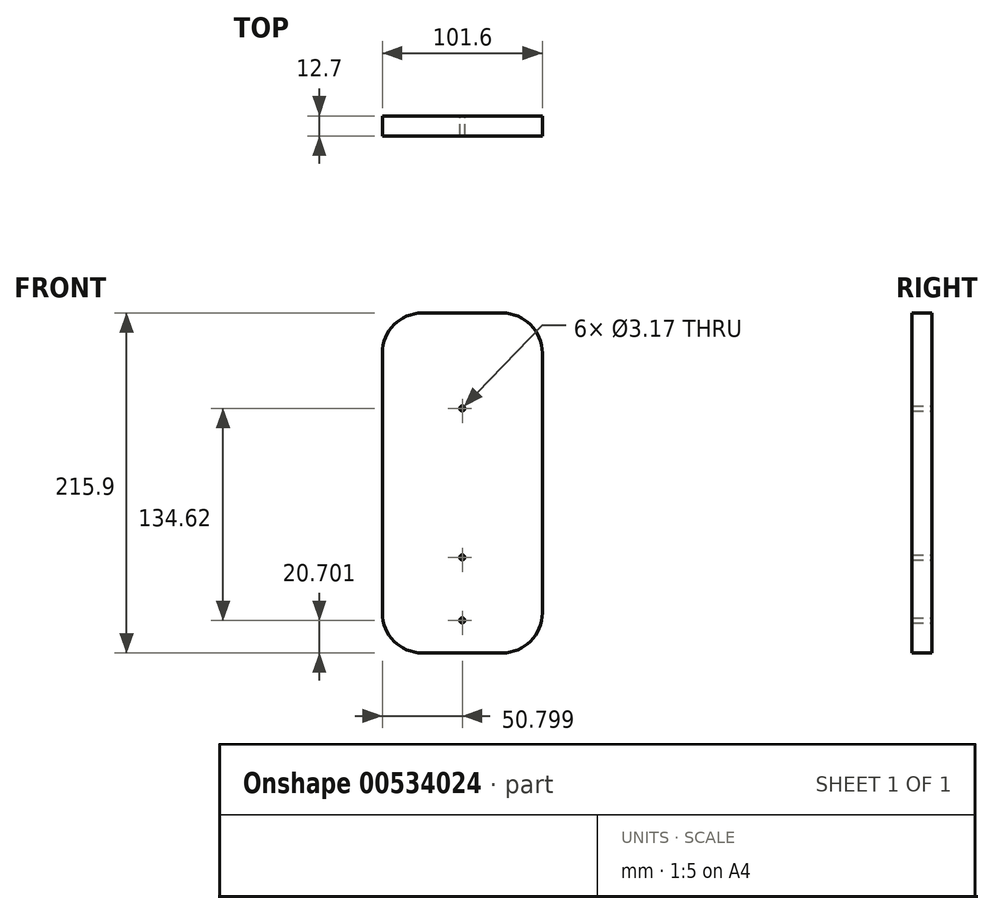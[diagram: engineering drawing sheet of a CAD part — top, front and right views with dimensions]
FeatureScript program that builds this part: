
annotation { "Feature Type Name" : "Feature", "Feature Type Description" : "" }
export const myFeature = defineFeature(function(context is Context, id is Id, definition is map)
    precondition{}
    {
        {
            var Q0;
            Q0=qCreatedBy(makeId("Front.planeOp"),FACE);
            var sketch = newSketch(context, id + "F0", { "sketchPlane" : qUnion([Q0])});
            skCircle(sketch, "E0", {"center": v(-90.61, -151.37) * mm, "radius": 8.9 * mm, "construction": true});
            skCircle(sketch, "E1", {"center": v(-90.61, -111.36) * mm, "radius": 31.12 * mm, "construction": true});
            skCircle(sketch, "E2", {"center": v(-90.61, -16.75) * mm, "radius": 63.5 * mm, "construction": true});
            skCircle(sketch, "E3", {"center": v(-90.61, -16.75) * mm, "radius": 1.59 * mm});
            skCircle(sketch, "E4", {"center": v(-90.61, -111.36) * mm, "radius": 1.59 * mm});
            skCircle(sketch, "E5", {"center": v(-90.61, -151.37) * mm, "radius": 1.59 * mm});
            skLineSegment(sketch, "E6.bottom", {"start": v(-141.41, -172.07) * mm, "end": v(-39.81, -172.07) * mm});
            skLineSegment(sketch, "E6.top", {"start": v(-141.41, 43.83) * mm, "end": v(-39.81, 43.83) * mm});
            skLineSegment(sketch, "E6.left", {"start": v(-141.41, -172.07) * mm, "end": v(-141.41, 43.83) * mm});
            skLineSegment(sketch, "E6.right", {"start": v(-39.81, -172.07) * mm, "end": v(-39.81, 43.83) * mm});
            skLineSegment(sketch, "E7", {"start": v(-90.61, 43.83) * mm, "end": v(-90.61, -172.07) * mm, "construction": true});
            skSolve(sketch);
        }
        {
            var Q0;
            Q0=makeQuery(id+"F0.imprint","IMPRINT",FACE,{"disambiguationData":[TD([[makeQuery(id+"F0.imprint","IMPRINT",EDGE,{"derivedFrom":sQuery(id+"F0.wireOp",EDGE,"E4")}),-1.0]])]});
            extrude(context, id + "F1", {"entities" : qUnion([Q0]), "depth" : 12.7 * mm, "offsetDistance" : 25.4 * mm});
        }
        {
            var Q0;
            Q0=makeQuery(id+"F1.opExtrude","SWEPT_EDGE",EDGE,{"disambiguationData":[OSD([sQuery(id+"F0.wireOp",EDGE,"E6.top"),sQuery(id+"F0.wireOp",EDGE,"E6.left")])]});
            fillet(context, id + "F2", {"entities" : qUnion([Q0]), "radius" : 25.4 * mm, "tangentPropagation" : true, "allowEdgeOverflow" : false});
        }
        {
            var Q0;
            Q0=makeQuery(id+"F1.opExtrude","SWEPT_EDGE",EDGE,{"disambiguationData":[OSD([sQuery(id+"F0.wireOp",EDGE,"E6.top"),sQuery(id+"F0.wireOp",EDGE,"E6.right")])]});
            fillet(context, id + "F3", {"entities" : qUnion([Q0]), "radius" : 25.4 * mm, "tangentPropagation" : true, "allowEdgeOverflow" : false});
        }
        {
            var Q0;
            Q0=makeQuery(id+"F1.opExtrude","SWEPT_EDGE",EDGE,{"disambiguationData":[OSD([sQuery(id+"F0.wireOp",EDGE,"E6.bottom"),sQuery(id+"F0.wireOp",EDGE,"E6.left")])]});
            fillet(context, id + "F4", {"entities" : qUnion([Q0]), "radius" : 25.4 * mm, "tangentPropagation" : true, "allowEdgeOverflow" : false});
        }
        {
            var Q0;
            Q0=makeQuery(id+"F1.opExtrude","SWEPT_EDGE",EDGE,{"disambiguationData":[OSD([sQuery(id+"F0.wireOp",EDGE,"E6.bottom"),sQuery(id+"F0.wireOp",EDGE,"E6.right")])]});
            fillet(context, id + "F5", {"entities" : qUnion([Q0]), "radius" : 25.4 * mm, "tangentPropagation" : true, "allowEdgeOverflow" : false});
        }
    });
